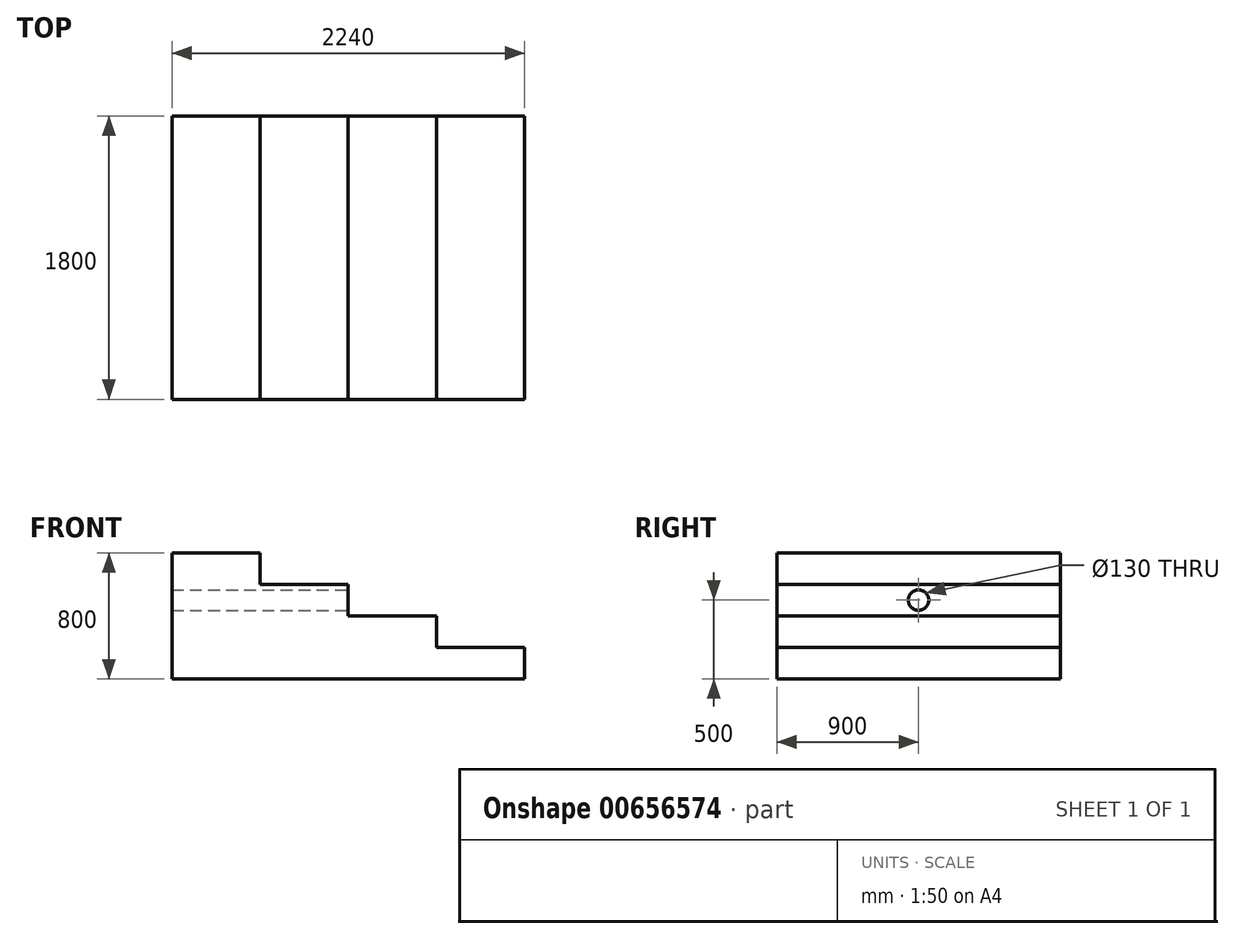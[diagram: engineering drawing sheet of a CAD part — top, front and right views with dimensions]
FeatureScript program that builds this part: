
annotation { "Feature Type Name" : "Feature", "Feature Type Description" : "" }
export const myFeature = defineFeature(function(context is Context, id is Id, definition is map)
    precondition{}
    {
        {
            var Q0;
            Q0=qCreatedBy(makeId("Top.planeOp"),FACE);
            var sketch = newSketch(context, id + "F0", { "sketchPlane" : qUnion([Q0])});
            skLineSegment(sketch, "E0.bottom", {"start": v(1120, -900) * mm, "end": v(-1120, -900) * mm});
            skLineSegment(sketch, "E0.top", {"start": v(1120, 900) * mm, "end": v(-1120, 900) * mm});
            skLineSegment(sketch, "E0.left", {"start": v(1120, -900) * mm, "end": v(1120, 900) * mm});
            skLineSegment(sketch, "E0.right", {"start": v(-1120, -900) * mm, "end": v(-1120, 900) * mm});
            skPoint(sketch, "E0.middle", {"position": v(0, 0) * mm});
            skSolve(sketch);
        }
        {
            var Q0;
            Q0=makeQuery(id+"F0.imprint","IMPRINT",FACE,{"disambiguationData":[TD([[makeQuery(id+"F0.imprint","IMPRINT",EDGE,{"derivedFrom":sQuery(id+"F0.wireOp",EDGE,"E0.bottom")}),-1.0]])]});
            extrude(context, id + "F1", {"entities" : qUnion([Q0]), "depth" : 200 * mm, "offsetDistance" : 25 * mm});
        }
        {
            var Q0;
            Q0=makeQuery(id+"F1.opExtrude","CAP_FACE",FACE,{"disambiguationData":[OSD([sQuery(id+"F0.wireOp",EDGE,"E0.bottom"),sQuery(id+"F0.wireOp",EDGE,"E0.top"),sQuery(id+"F0.wireOp",EDGE,"E0.left"),sQuery(id+"F0.wireOp",EDGE,"E0.right")])],"isStart":false});
            var sketch = newSketch(context, id + "F2", { "sketchPlane" : qUnion([Q0])});
            skLineSegment(sketch, "E1.bottom", {"start": v(-1120, 900) * mm, "end": v(560, 900) * mm});
            skLineSegment(sketch, "E1.top", {"start": v(-1120, -900) * mm, "end": v(560, -900) * mm});
            skLineSegment(sketch, "E1.left", {"start": v(-1120, 900) * mm, "end": v(-1120, -900) * mm});
            skLineSegment(sketch, "E1.right", {"start": v(560, 900) * mm, "end": v(560, -900) * mm});
            skSolve(sketch);
        }
        {
            var Q0;
            Q0 = qSketchRegion(id + "F2", true);
            extrude(context, id + "F3", {"entities" : qUnion([Q0]), "operationType" : NewBodyOperationType.ADD, "depth" : 200 * mm, "offsetDistance" : 25 * mm});
        }
        {
            var Q0;
            Q0=makeQuery(id+"F3.opExtrude","CAP_FACE",FACE,{"disambiguationData":[OSD([sQuery(id+"F2.wireOp",EDGE,"E1.bottom"),sQuery(id+"F2.wireOp",EDGE,"E1.top"),sQuery(id+"F2.wireOp",EDGE,"E1.left"),sQuery(id+"F2.wireOp",EDGE,"E1.right")])],"isStart":false});
            var sketch = newSketch(context, id + "F4", { "sketchPlane" : qUnion([Q0])});
            skLineSegment(sketch, "E2.bottom", {"start": v(-1120, 900) * mm, "end": v(0, 900) * mm});
            skLineSegment(sketch, "E2.top", {"start": v(-1120, -900) * mm, "end": v(0, -900) * mm});
            skLineSegment(sketch, "E2.left", {"start": v(-1120, 900) * mm, "end": v(-1120, -900) * mm});
            skLineSegment(sketch, "E2.right", {"start": v(0, 900) * mm, "end": v(0, -900) * mm});
            skSolve(sketch);
        }
        {
            var Q0;
            Q0 = qSketchRegion(id + "F4", true);
            extrude(context, id + "F5", {"entities" : qUnion([Q0]), "operationType" : NewBodyOperationType.ADD, "depth" : 200 * mm, "offsetDistance" : 25 * mm});
        }
        {
            var Q0;
            Q0=makeQuery(id+"F5.opExtrude","CAP_FACE",FACE,{"disambiguationData":[OSD([sQuery(id+"F4.wireOp",EDGE,"E2.bottom"),sQuery(id+"F4.wireOp",EDGE,"E2.top"),sQuery(id+"F4.wireOp",EDGE,"E2.left"),sQuery(id+"F4.wireOp",EDGE,"E2.right")])],"isStart":false});
            var sketch = newSketch(context, id + "F6", { "sketchPlane" : qUnion([Q0])});
            skLineSegment(sketch, "E3.bottom", {"start": v(-1120, 900) * mm, "end": v(-560, 900) * mm});
            skLineSegment(sketch, "E3.top", {"start": v(-1120, -900) * mm, "end": v(-560, -900) * mm});
            skLineSegment(sketch, "E3.left", {"start": v(-1120, 900) * mm, "end": v(-1120, -900) * mm});
            skLineSegment(sketch, "E3.right", {"start": v(-560, 900) * mm, "end": v(-560, -900) * mm});
            skSolve(sketch);
        }
        {
            var Q0;
            Q0=makeQuery(id+"F6.imprint","IMPRINT",FACE,{"disambiguationData":[TD([[makeQuery(id+"F6.imprint","IMPRINT",EDGE,{"derivedFrom":sQuery(id+"F6.wireOp",EDGE,"E3.bottom")}),1.0]])]});
            extrude(context, id + "F7", {"entities" : qUnion([Q0]), "operationType" : NewBodyOperationType.ADD, "depth" : 200 * mm, "offsetDistance" : 25 * mm});
        }
        {
            var Q0;
            Q0=makeQuery(id+"F5.opExtrude","SWEPT_FACE",FACE,{"disambiguationData":[OSD([sQuery(id+"F4.wireOp",EDGE,"E2.right")])]});
            var sketch = newSketch(context, id + "F8", { "sketchPlane" : qUnion([Q0])});
            skPoint(sketch, "E4.oppositeSnap0", {"position": v(900, 500) * mm});
            skPoint(sketch, "E4.oppositeSnap1", {"position": v(0, 600) * mm});
            skLineSegment(sketch, "E4.bottom", {"start": v(900, 600) * mm, "end": v(0, 600) * mm});
            skLineSegment(sketch, "E4.top", {"start": v(900, 500) * mm, "end": v(0, 500) * mm});
            skLineSegment(sketch, "E4.left", {"start": v(900, 600) * mm, "end": v(900, 500) * mm});
            skLineSegment(sketch, "E4.right", {"start": v(0, 600) * mm, "end": v(0, 500) * mm});
            skCircle(sketch, "E5", {"center": v(0, 500) * mm, "radius": 65 * mm});
            skSolve(sketch);
        }
        {
            var Q0;
            {var subQ0=sQuery(id+"F8.wireOp",EDGE,"E4.right");var subQ1=sQuery(id+"F8.wireOp",EDGE,"E4.top");var subQ2=makeQuery(id+"F8.imprint","INTERSECT",VERTEX,{"derivedFrom":[subQ1,subQ0]});Q0=makeQuery(id+"F8.imprint","IMPRINT",FACE,{"disambiguationData":[TD([[makeQuery(id+"F8.imprint","IMPRINT",EDGE,{"disambiguationData":[TD([[subQ2,1.0]])],"derivedFrom":subQ1}),-1.0]])]});}
            var Q1;
            {var subQ0=sQuery(id+"F8.wireOp",EDGE,"E4.right");var subQ1=sQuery(id+"F8.wireOp",EDGE,"E4.top");var subQ2=makeQuery(id+"F8.imprint","INTERSECT",VERTEX,{"derivedFrom":[subQ1,subQ0]});Q1=makeQuery(id+"F8.imprint","IMPRINT",FACE,{"disambiguationData":[TD([[makeQuery(id+"F8.imprint","IMPRINT",EDGE,{"disambiguationData":[TD([[subQ2,1.0]])],"derivedFrom":subQ1}),1.0]])]});}
            extrude(context, id + "F9", {"entities" : qUnion([Q0, Q1]), "operationType" : NewBodyOperationType.REMOVE, "oppositeDirection" : true, "depth" : 1120 * mm, "offsetDistance" : 25 * mm});
        }
    });
